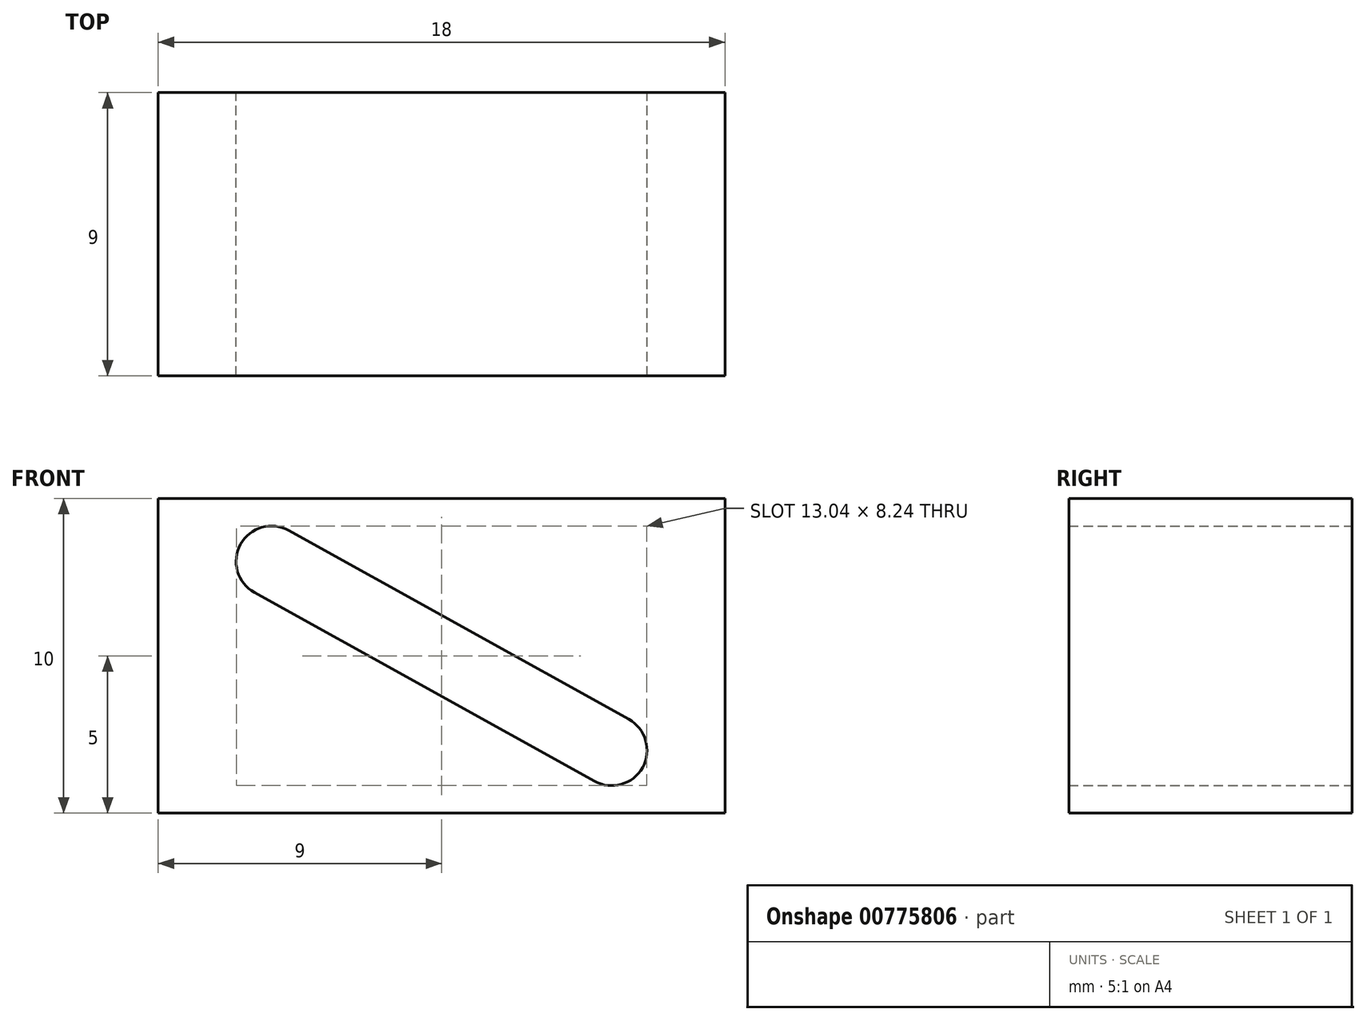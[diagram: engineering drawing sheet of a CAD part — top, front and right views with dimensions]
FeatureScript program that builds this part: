
annotation { "Feature Type Name" : "Feature", "Feature Type Description" : "" }
export const myFeature = defineFeature(function(context is Context, id is Id, definition is map)
    precondition{}
    {
        {
            var Q0;
            Q0=qCreatedBy(makeId("Front.planeOp"),FACE);
            var sketch = newSketch(context, id + "F0", { "sketchPlane" : qUnion([Q0])});
            skLineSegment(sketch, "E0.bottom", {"start": v(-9, 5) * mm, "end": v(9, 5) * mm});
            skLineSegment(sketch, "E0.top", {"start": v(-9, -5) * mm, "end": v(9, -5) * mm});
            skLineSegment(sketch, "E0.left", {"start": v(-9, 5) * mm, "end": v(-9, -5) * mm});
            skLineSegment(sketch, "E0.right", {"start": v(9, 5) * mm, "end": v(9, -5) * mm});
            skPoint(sketch, "E0.middle", {"position": v(0, 0) * mm});
            skLineSegment(sketch, "E1", {"start": v(9, -5) * mm, "end": v(-9, 5) * mm, "construction": true});
            skPoint(sketch, "E2", {"position": v(-5.4, 3) * mm});
            skPoint(sketch, "E3", {"position": v(5.4, -3) * mm});
            skArc(sketch, "E4", {"start": v(-4.85, 3.98) * mm, "mid": v(-6.38, 3.55) * mm, "end": v(-5.95, 2.02) * mm});
            skArc(sketch, "E5", {"start": v(4.85, -3.98) * mm, "mid": v(6.38, -3.55) * mm, "end": v(5.95, -2.02) * mm});
            skLineSegment(sketch, "E6", {"start": v(-5.95, 2.02) * mm, "end": v(4.85, -3.98) * mm});
            skLineSegment(sketch, "E7", {"start": v(-4.85, 3.98) * mm, "end": v(5.95, -2.02) * mm});
            skSolve(sketch);
        }
        {
            var Q0;
            Q0=makeQuery(id+"F0.imprint","IMPRINT",FACE,{"disambiguationData":[TD([[makeQuery(id+"F0.imprint","IMPRINT",EDGE,{"derivedFrom":sQuery(id+"F0.wireOp",EDGE,"E0.bottom")}),-1.0]])]});
            extrude(context, id + "F1", {"entities" : qUnion([Q0]), "endBound" : BoundingType.SYMMETRIC, "depth" : 9 * mm, "offsetDistance" : 25 * mm});
        }
    });
